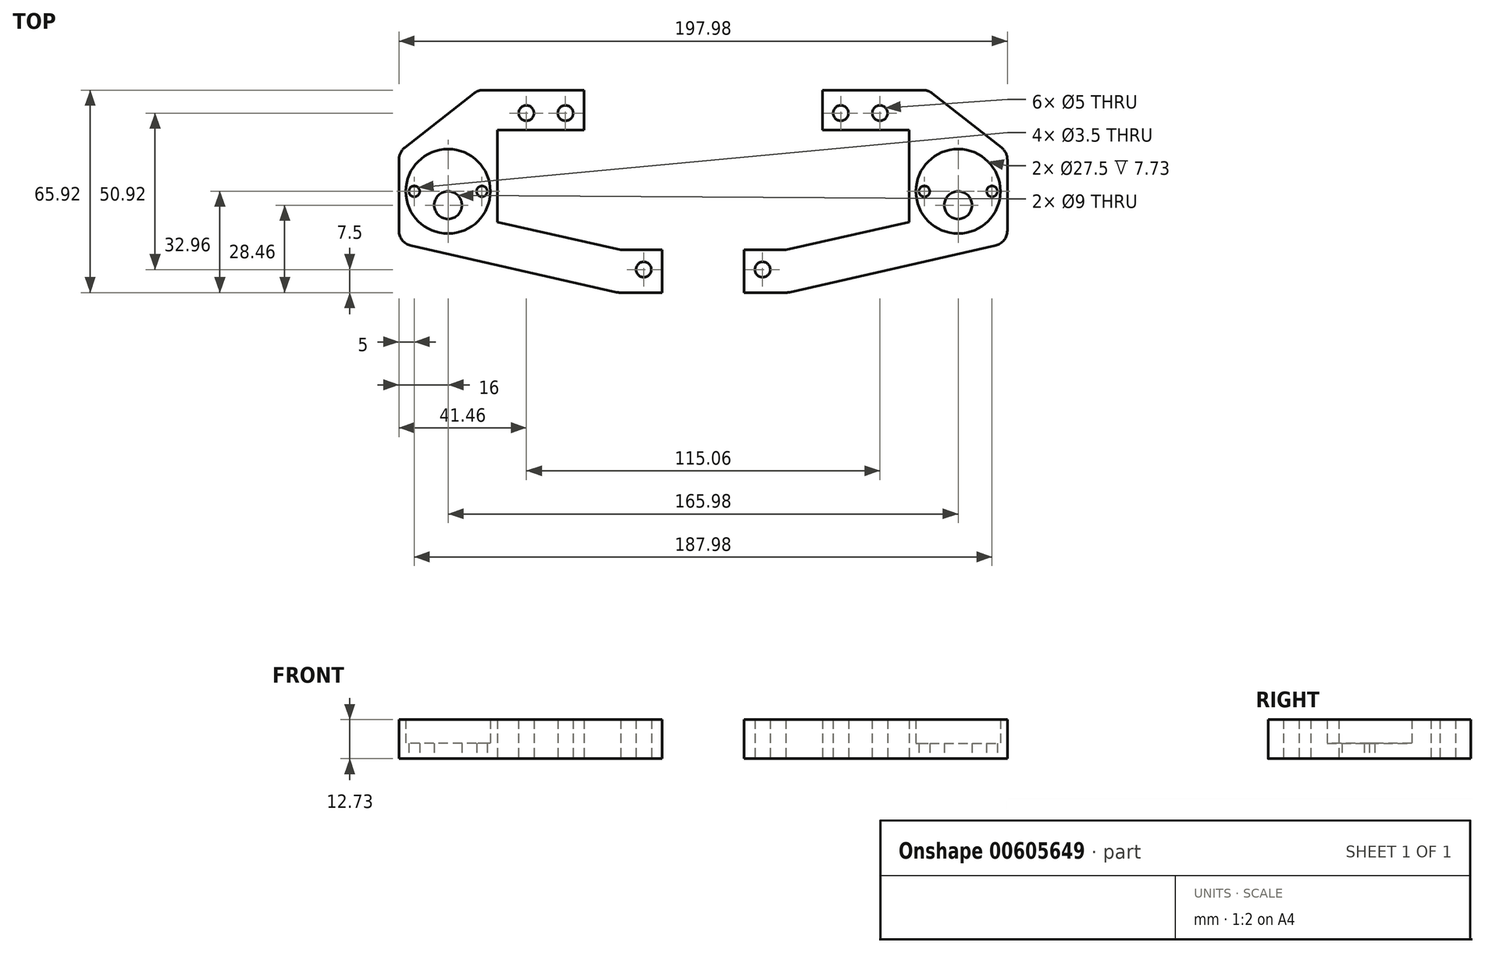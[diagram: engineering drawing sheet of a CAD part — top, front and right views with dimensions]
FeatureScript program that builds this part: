
annotation { "Feature Type Name" : "Feature", "Feature Type Description" : "" }
export const myFeature = defineFeature(function(context is Context, id is Id, definition is map)
    precondition{}
    {
        {
            var Q0;
            Q0=qCreatedBy(makeId("Top.planeOp"),FACE);
            var sketch = newSketch(context, id + "F0", { "sketchPlane" : qUnion([Q0])});
            skPoint(sketch, "E0", {"position": v(0, 0) * mm});
            skPoint(sketch, "E1", {"position": v(0, -50.92) * mm});
            skPoint(sketch, "E2", {"position": v(25.46, -50.92) * mm});
            skPoint(sketch, "E3", {"position": v(-12.73, 0) * mm});
            skPoint(sketch, "E4", {"position": v(0, -25.46) * mm});
            skPoint(sketch, "E5", {"position": v(-38.2, -25.46) * mm});
            skPoint(sketch, "E6.start.orphan", {"position": v(6, 0) * mm});
            skLineSegment(sketch, "E7", {"start": v(6, 5.5) * mm, "end": v(6, -5.5) * mm});
            skLineSegment(sketch, "E8", {"start": v(31.46, -44.53) * mm, "end": v(17.95, -44.53) * mm});
            skCircle(sketch, "E9", {"center": v(-12.73, 0) * mm, "radius": 2.5 * mm});
            skCircle(sketch, "E10", {"center": v(0, 0) * mm, "radius": 2.5 * mm});
            skCircle(sketch, "E11", {"center": v(25.46, -50.92) * mm, "radius": 2.5 * mm});
            skPoint(sketch, "E12", {"position": v(6, 7.5) * mm});
            skLineSegment(sketch, "E13", {"start": v(6, 7.5) * mm, "end": v(6, 5.5) * mm});
            skLineSegment(sketch, "E14", {"start": v(17.2, -58.42) * mm, "end": v(31.46, -58.42) * mm});
            skPoint(sketch, "E15", {"position": v(31.46, -50.92) * mm});
            skLineSegment(sketch, "E16", {"start": v(31.46, -44.53) * mm, "end": v(31.46, -58.42) * mm});
            skPoint(sketch, "E17", {"position": v(31.46, -44.53) * mm});
            skPoint(sketch, "E18", {"position": v(31.46, -58.42) * mm});
            skLineSegment(sketch, "E19", {"start": v(6, 7.5) * mm, "end": v(-28.42, 7.5) * mm});
            skCircle(sketch, "E20.0", {"center": v(-38.2, -25.46) * mm, "radius": 16 * mm});
            skLineSegment(sketch, "E21", {"start": v(-38.2, -25.46) * mm, "end": v(-54.2, -25.46) * mm, "construction": true});
            skLineSegment(sketch, "E22", {"start": v(-54.2, -25.46) * mm, "end": v(-54.2, -42.24) * mm});
            skLineSegment(sketch, "E23", {"start": v(-28.42, 7.5) * mm, "end": v(-54.2, -12.73) * mm});
            skLineSegment(sketch, "E24", {"start": v(-38.2, -25.46) * mm, "end": v(-22.2, -25.46) * mm, "construction": true});
            skLineSegment(sketch, "E25", {"start": v(-22.2, -25.46) * mm, "end": v(-22.2, -5.5) * mm});
            skLineSegment(sketch, "E26", {"start": v(-22.2, -25.46) * mm, "end": v(-22.2, -35.43) * mm});
            skLineSegment(sketch, "E27", {"start": v(-54.2, -12.73) * mm, "end": v(-54.2, -25.46) * mm});
            skLineSegment(sketch, "E28", {"start": v(-22.2, -35.43) * mm, "end": v(17.95, -44.53) * mm});
            skLineSegment(sketch, "E29", {"start": v(17.2, -58.42) * mm, "end": v(-54.2, -42.24) * mm});
            skLineSegment(sketch, "E30", {"start": v(-22.2, -5.5) * mm, "end": v(6, -5.5) * mm});
            skPoint(sketch, "E31", {"position": v(-38.2, -29.96) * mm});
            skCircle(sketch, "E32", {"center": v(-38.2, -25.46) * mm, "radius": 13.75 * mm});
            skCircle(sketch, "E33", {"center": v(-38.2, -29.96) * mm, "radius": 4.5 * mm});
            skPoint(sketch, "E34", {"position": v(-49.19, -25.46) * mm});
            skPoint(sketch, "E35", {"position": v(-27.2, -25.46) * mm});
            skCircle(sketch, "E36", {"center": v(-49.19, -25.46) * mm, "radius": 1.75 * mm});
            skCircle(sketch, "E37", {"center": v(-27.2, -25.46) * mm, "radius": 1.75 * mm});
            skSolve(sketch);
        }
        {
            var Q0;
            Q0=makeQuery(id+"F0.imprint","IMPRINT",FACE,{"disambiguationData":[TD([[makeQuery(id+"F0.imprint","IMPRINT",EDGE,{"derivedFrom":sQuery(id+"F0.wireOp",EDGE,"E8")}),1.0]])]});
            var Q1;
            Q1=makeQuery(id+"F0.imprint","IMPRINT",FACE,{"disambiguationData":[TD([[makeQuery(id+"F0.imprint","IMPRINT",EDGE,{"derivedFrom":sQuery(id+"F0.wireOp",EDGE,"E7")}),-1.0]])]});
            var Q2;
            Q2=makeQuery(id+"F0.imprint","IMPRINT",FACE,{"disambiguationData":[TD([[makeQuery(id+"F0.imprint","IMPRINT",EDGE,{"derivedFrom":sQuery(id+"F0.wireOp",EDGE,"E32")}),-1.0]])]});
            extrude(context, id + "F1", {"entities" : qUnion([Q0, Q1, Q2]), "depth" : 12.73 * mm, "offsetDistance" : 25 * mm});
        }
        {
            var Q0;
            Q0=makeQuery(id+"F0.imprint","IMPRINT",FACE,{"disambiguationData":[TD([[makeQuery(id+"F0.imprint","IMPRINT",EDGE,{"derivedFrom":sQuery(id+"F0.wireOp",EDGE,"E32")}),1.0]])]});
            extrude(context, id + "F2", {"entities" : qUnion([Q0]), "operationType" : NewBodyOperationType.ADD, "depth" : 5 * mm, "offsetDistance" : 25 * mm});
        }
        {
            var Q0;
            Q0=makeQuery(id+"F1.opExtrude","SWEPT_EDGE",EDGE,{"disambiguationData":[OSD([sQuery(id+"F0.wireOp",EDGE,"E14"),sQuery(id+"F0.wireOp",EDGE,"E29")])]});
            var Q1;
            Q1=makeQuery(id+"F1.opExtrude","SWEPT_EDGE",EDGE,{"disambiguationData":[OSD([sQuery(id+"F0.wireOp",EDGE,"E22"),sQuery(id+"F0.wireOp",EDGE,"E29")])]});
            var Q2;
            Q2=makeQuery(id+"F1.opExtrude","SWEPT_EDGE",EDGE,{"disambiguationData":[OSD([sQuery(id+"F0.wireOp",EDGE,"E23"),sQuery(id+"F0.wireOp",EDGE,"E27")])]});
            var Q3;
            Q3=makeQuery(id+"F1.opExtrude","SWEPT_EDGE",EDGE,{"disambiguationData":[OSD([sQuery(id+"F0.wireOp",EDGE,"E19"),sQuery(id+"F0.wireOp",EDGE,"E23")])]});
            fillet(context, id + "F3", {"entities" : qUnion([Q0, Q1, Q2, Q3]), "radius" : 5 * mm, "tangentPropagation" : true, "allowEdgeOverflow" : false});
        }
        {
            var Q0;
            Q0=makeQuery(id+"F1.opExtrude","SWEPT_BODY",BODY,{"disambiguationData":[OSD([sQuery(id+"F0.wireOp",EDGE,"E7"),sQuery(id+"F0.wireOp",EDGE,"E8"),sQuery(id+"F0.wireOp",EDGE,"E9"),sQuery(id+"F0.wireOp",EDGE,"E10"),sQuery(id+"F0.wireOp",EDGE,"E11"),sQuery(id+"F0.wireOp",EDGE,"E13"),sQuery(id+"F0.wireOp",EDGE,"E14"),sQuery(id+"F0.wireOp",EDGE,"E16"),sQuery(id+"F0.wireOp",EDGE,"E19"),sQuery(id+"F0.wireOp",EDGE,"E22"),sQuery(id+"F0.wireOp",EDGE,"E23"),sQuery(id+"F0.wireOp",EDGE,"E25"),sQuery(id+"F0.wireOp",EDGE,"E26"),sQuery(id+"F0.wireOp",EDGE,"E27"),sQuery(id+"F0.wireOp",EDGE,"E28"),sQuery(id+"F0.wireOp",EDGE,"E29"),sQuery(id+"F0.wireOp",EDGE,"E30"),sQuery(id+"F0.wireOp",EDGE,"E32")])]});
            transform(context, id + "F4", {"entities" : qUnion([Q0]), "transformType" : TransformType.TRANSLATION_3D, "dx" : -44.8 * mm, "dy" : 0 * mm, "dz" : 0 * mm, "makeCopy" : false});
        }
        {
            var Q0;
            Q0=makeQuery(id+"F1.opExtrude","SWEPT_BODY",BODY,{"disambiguationData":[OSD([sQuery(id+"F0.wireOp",EDGE,"E7"),sQuery(id+"F0.wireOp",EDGE,"E8"),sQuery(id+"F0.wireOp",EDGE,"E9"),sQuery(id+"F0.wireOp",EDGE,"E10"),sQuery(id+"F0.wireOp",EDGE,"E11"),sQuery(id+"F0.wireOp",EDGE,"E13"),sQuery(id+"F0.wireOp",EDGE,"E14"),sQuery(id+"F0.wireOp",EDGE,"E16"),sQuery(id+"F0.wireOp",EDGE,"E19"),sQuery(id+"F0.wireOp",EDGE,"E22"),sQuery(id+"F0.wireOp",EDGE,"E23"),sQuery(id+"F0.wireOp",EDGE,"E25"),sQuery(id+"F0.wireOp",EDGE,"E26"),sQuery(id+"F0.wireOp",EDGE,"E27"),sQuery(id+"F0.wireOp",EDGE,"E28"),sQuery(id+"F0.wireOp",EDGE,"E29"),sQuery(id+"F0.wireOp",EDGE,"E30"),sQuery(id+"F0.wireOp",EDGE,"E32")])]});
            var Q1;
            Q1=qCreatedBy(makeId("Right.planeOp"),FACE);
            mirror(context, id + "F5", {"entities" : qUnion([Q0]), "mirrorPlane" : qUnion([Q1])});
        }
    });
